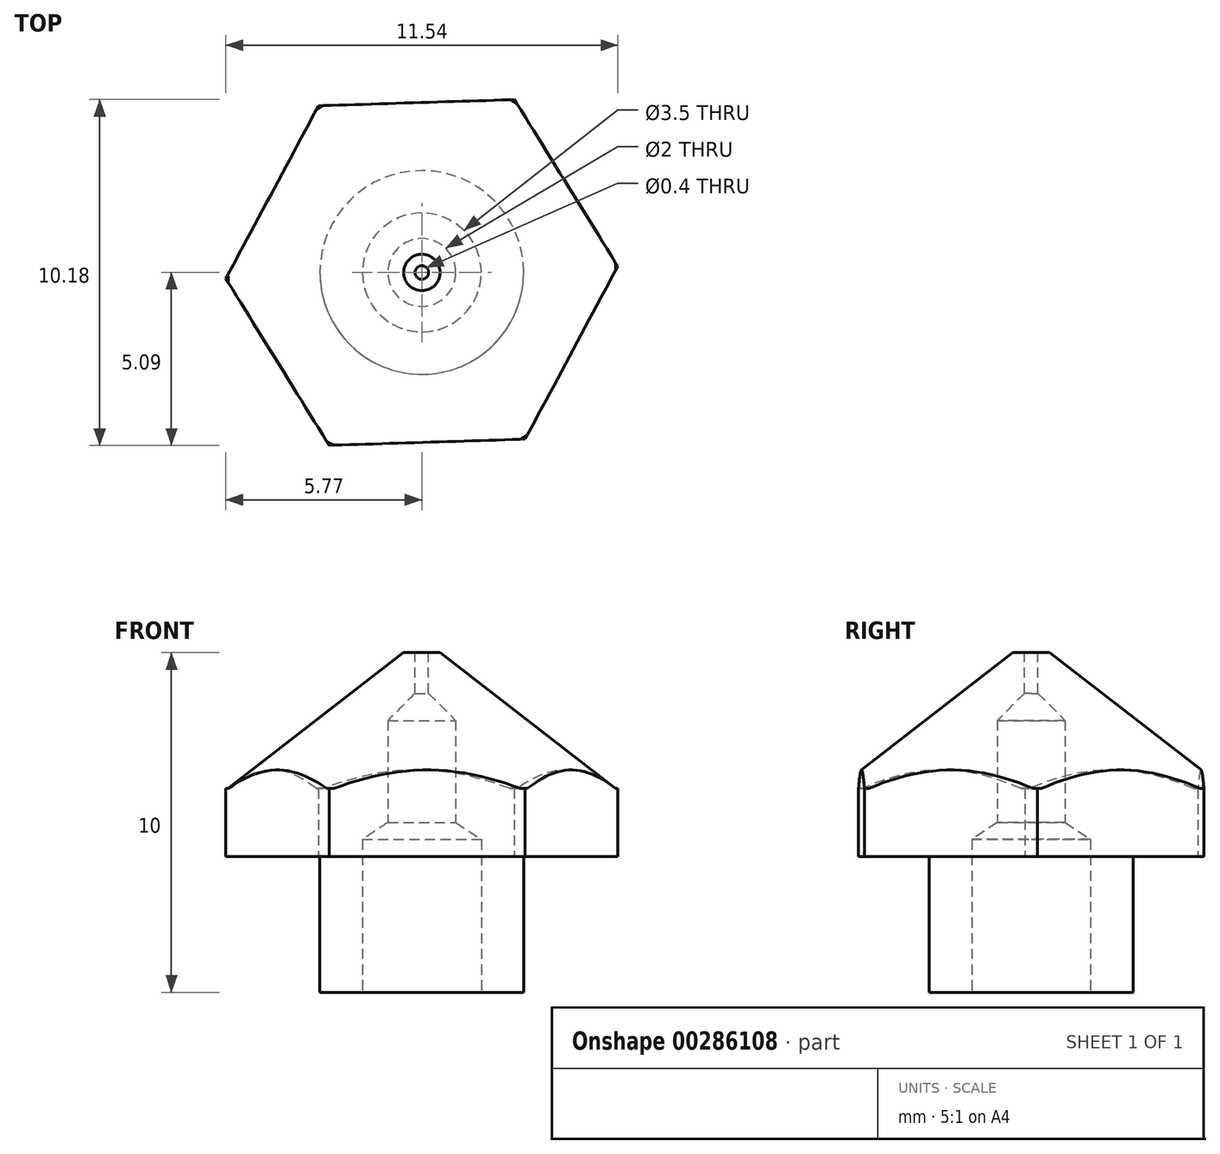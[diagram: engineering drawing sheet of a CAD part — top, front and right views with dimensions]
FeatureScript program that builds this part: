
annotation { "Feature Type Name" : "Feature", "Feature Type Description" : "" }
export const myFeature = defineFeature(function(context is Context, id is Id, definition is map)
    precondition{}
    {
        {
            var Q0;
            Q0=qCreatedBy(makeId("Top.planeOp"),FACE);
            var sketch = newSketch(context, id + "F0", { "sketchPlane" : qUnion([Q0])});
            skCircle(sketch, "E0.cCircle", {"center": v(0, 0) * mm, "radius": 5 * mm, "construction": true});
            skLineSegment(sketch, "E0.0", {"start": v(2.73, 5.09) * mm, "end": v(5.77, 0.18) * mm});
            skLineSegment(sketch, "E0.1", {"start": v(5.77, 0.18) * mm, "end": v(3.04, -4.9) * mm});
            skLineSegment(sketch, "E0.2", {"start": v(3.04, -4.9) * mm, "end": v(-2.73, -5.09) * mm});
            skLineSegment(sketch, "E0.3", {"start": v(-2.73, -5.09) * mm, "end": v(-5.77, -0.18) * mm});
            skLineSegment(sketch, "E0.4", {"start": v(-5.77, -0.18) * mm, "end": v(-3.04, 4.9) * mm});
            skLineSegment(sketch, "E0.5", {"start": v(-3.04, 4.9) * mm, "end": v(2.73, 5.09) * mm});
            skPoint(sketch, "E0.0.midPoint", {"position": v(4.25, 2.64) * mm});
            skSolve(sketch);
        }
        {
            var Q0;
            Q0=qSketchRegion(id+"F0",true);
            extrude(context, id + "F1", {"entities" : qUnion([Q0]), "depth" : 10 * mm});
        }
        {
            var Q0;
            Q0=qCreatedBy(makeId("Front.planeOp"),FACE);
            var sketch = newSketch(context, id + "F2", { "sketchPlane" : qUnion([Q0])});
            skLineSegment(sketch, "E1", {"start": v(0, 13.03) * mm, "end": v(0, -6.4) * mm, "construction": true});
            skLineSegment(sketch, "E2.bottom", {"start": v(3, 4) * mm, "end": v(7.67, 4) * mm});
            skLineSegment(sketch, "E2.top", {"start": v(3, -2.32) * mm, "end": v(7.67, -2.32) * mm});
            skLineSegment(sketch, "E2.left", {"start": v(3, 4) * mm, "end": v(3, -2.32) * mm});
            skLineSegment(sketch, "E2.right", {"start": v(7.67, 4) * mm, "end": v(7.67, -2.32) * mm});
            skLineSegment(sketch, "E3", {"start": v(0.4, 10.1) * mm, "end": v(5.7, 6) * mm});
            skLineSegment(sketch, "E4", {"start": v(5.7, 6) * mm, "end": v(7.53, 6) * mm});
            skLineSegment(sketch, "E5", {"start": v(7.53, 6) * mm, "end": v(7.53, 10.88) * mm});
            skLineSegment(sketch, "E6", {"start": v(7.53, 10.88) * mm, "end": v(0.4, 10.88) * mm});
            skLineSegment(sketch, "E7", {"start": v(0.4, 10.88) * mm, "end": v(0.4, 10.1) * mm});
            skLineSegment(sketch, "E8", {"start": v(0, -1.97) * mm, "end": v(1.75, -1.97) * mm});
            skLineSegment(sketch, "E9", {"start": v(1.75, -1.97) * mm, "end": v(1.75, 4.5) * mm});
            skLineSegment(sketch, "E10", {"start": v(1.75, 4.5) * mm, "end": v(1, 5) * mm});
            skLineSegment(sketch, "E11", {"start": v(1, 5) * mm, "end": v(1, 8) * mm});
            skLineSegment(sketch, "E12", {"start": v(1, 8) * mm, "end": v(0, 9) * mm});
            skLineSegment(sketch, "E13", {"start": v(0, 9) * mm, "end": v(0, -1.97) * mm});
            skSolve(sketch);
        }
        {
            var Q0;
            Q0=qSketchRegion(id+"F2",true);
            var Q1;
            Q1=sQuery(id+"F2.wireOp",EDGE,"E1");
            revolve(context, id + "F3", {"operationType" : NewBodyOperationType.REMOVE, "entities" : qUnion([Q0]), "axis" : qUnion([Q1]), "revolveType" : RevolveType.FULL, "oppositeDirection" : true});
        }
        {
            var Q0;
            Q0=makeQuery(id+"F1.opExtrude","CAP_FACE",FACE,{"disambiguationData":[OSD([sQuery(id+"F0.wireOp",EDGE,"E0.0"),sQuery(id+"F0.wireOp",EDGE,"E0.1"),sQuery(id+"F0.wireOp",EDGE,"E0.2"),sQuery(id+"F0.wireOp",EDGE,"E0.3"),sQuery(id+"F0.wireOp",EDGE,"E0.4"),sQuery(id+"F0.wireOp",EDGE,"E0.5")])],"isStart":false});
            var sketch = newSketch(context, id + "F4", { "sketchPlane" : qUnion([Q0])});
            skCircle(sketch, "E14", {"center": v(0, 0) * mm, "radius": 0.2 * mm});
            skSolve(sketch);
        }
        {
            var Q0;
            Q0=qSketchRegion(id+"F4",true);
            extrude(context, id + "F5", {"entities" : qUnion([Q0]), "operationType" : NewBodyOperationType.REMOVE, "endBound" : BoundingType.THROUGH_ALL, "oppositeDirection" : true, "depth" : 25 * mm});
        }
    });
